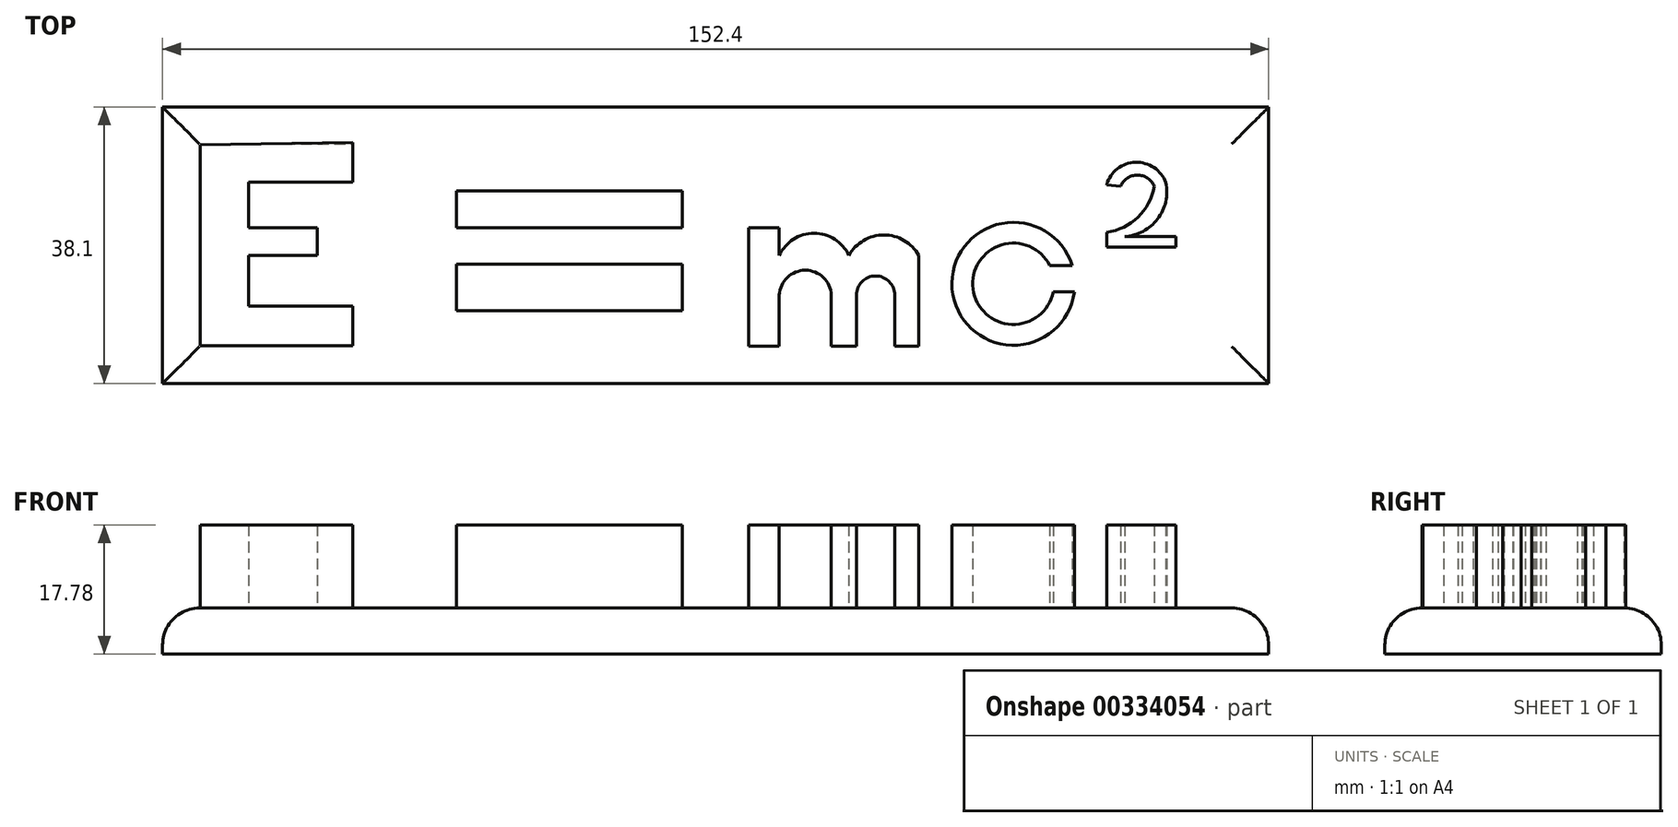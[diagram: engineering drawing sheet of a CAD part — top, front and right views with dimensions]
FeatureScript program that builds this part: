
annotation { "Feature Type Name" : "Feature", "Feature Type Description" : "" }
export const myFeature = defineFeature(function(context is Context, id is Id, definition is map)
    precondition{}
    {
        {
            var Q0;
            Q0=qCreatedBy(makeId("Top.planeOp"),FACE);
            var sketch = newSketch(context, id + "F0", { "sketchPlane" : qUnion([Q0])});
            skLineSegment(sketch, "E0", {"start": v(-76.78, -21.49) * mm, "end": v(75.62, -21.49) * mm});
            skLineSegment(sketch, "E1", {"start": v(-76.78, -21.49) * mm, "end": v(-76.78, 16.61) * mm});
            skLineSegment(sketch, "E2", {"start": v(-76.78, 16.61) * mm, "end": v(75.62, 16.61) * mm});
            skLineSegment(sketch, "E3", {"start": v(75.62, 16.61) * mm, "end": v(75.62, -21.49) * mm});
            skSolve(sketch);
        }
        {
            var Q0;
            Q0 = qSketchRegion(id + "F0", true);
            extrude(context, id + "F1", {"entities" : qUnion([Q0]), "depth" : 6.35 * mm});
        }
        {
            var Q0;
            Q0=makeQuery(id+"F1.opExtrude","CAP_FACE",FACE,{"disambiguationData":[OSD([sQuery(id+"F0.wireOp",EDGE,"E0"),sQuery(id+"F0.wireOp",EDGE,"E1"),sQuery(id+"F0.wireOp",EDGE,"E2"),sQuery(id+"F0.wireOp",EDGE,"E3")])],"isStart":false});
            fillet(context, id + "F2", {"entities" : qUnion([Q0]), "radius" : 5.08 * mm, "tangentPropagation" : true, "allowEdgeOverflow" : false});
        }
        {
            var Q0;
            Q0=makeQuery(id+"F1.opExtrude","CAP_FACE",FACE,{"disambiguationData":[OSD([sQuery(id+"F0.wireOp",EDGE,"E0"),sQuery(id+"F0.wireOp",EDGE,"E1"),sQuery(id+"F0.wireOp",EDGE,"E2"),sQuery(id+"F0.wireOp",EDGE,"E3")])],"isStart":false});
            var sketch = newSketch(context, id + "F3", { "sketchPlane" : qUnion([Q0])});
            skLineSegment(sketch, "E4", {"start": v(-71.61, 11.43) * mm, "end": v(-71.61, -16.3) * mm});
            skLineSegment(sketch, "E5", {"start": v(-71.61, -16.3) * mm, "end": v(-50.58, -16.3) * mm});
            skLineSegment(sketch, "E6", {"start": v(-50.58, -16.3) * mm, "end": v(-50.58, -10.82) * mm});
            skLineSegment(sketch, "E7", {"start": v(-50.58, -10.82) * mm, "end": v(-64.9, -10.82) * mm});
            skLineSegment(sketch, "E8", {"start": v(-64.9, -10.82) * mm, "end": v(-64.9, -3.81) * mm});
            skLineSegment(sketch, "E9", {"start": v(-64.9, -3.81) * mm, "end": v(-55.46, -3.81) * mm});
            skLineSegment(sketch, "E10", {"start": v(-55.46, -3.81) * mm, "end": v(-55.46, 0) * mm});
            skLineSegment(sketch, "E11", {"start": v(-64.9, 0) * mm, "end": v(-64.9, 6.25) * mm});
            skLineSegment(sketch, "E12", {"start": v(-64.9, 6.25) * mm, "end": v(-50.58, 6.25) * mm});
            skLineSegment(sketch, "E13", {"start": v(-50.58, 6.25) * mm, "end": v(-50.58, 11.73) * mm});
            skLineSegment(sketch, "E14", {"start": v(-50.58, 11.73) * mm, "end": v(-71.61, 11.43) * mm});
            skLineSegment(sketch, "E15", {"start": v(-64.9, 0) * mm, "end": v(-55.46, 0) * mm});
            skSolve(sketch);
        }
        {
            var Q0;
            Q0 = qSketchRegion(id + "F3", true);
            extrude(context, id + "F4", {"entities" : qUnion([Q0]), "operationType" : NewBodyOperationType.ADD, "depth" : 11.43 * mm});
        }
        {
            var Q0;
            Q0=makeQuery(id+"F1.opExtrude","CAP_FACE",FACE,{"disambiguationData":[OSD([sQuery(id+"F0.wireOp",EDGE,"E0"),sQuery(id+"F0.wireOp",EDGE,"E1"),sQuery(id+"F0.wireOp",EDGE,"E2"),sQuery(id+"F0.wireOp",EDGE,"E3")])],"isStart":false});
            var sketch = newSketch(context, id + "F5", { "sketchPlane" : qUnion([Q0])});
            skLineSegment(sketch, "E16", {"start": v(-36.26, 5.03) * mm, "end": v(-36.26, 0) * mm});
            skLineSegment(sketch, "E17", {"start": v(-36.26, 5.03) * mm, "end": v(-5.17, 5.03) * mm});
            skLineSegment(sketch, "E18", {"start": v(-5.17, 5.03) * mm, "end": v(-5.17, 0) * mm});
            skLineSegment(sketch, "E19", {"start": v(-5.17, 0) * mm, "end": v(-36.26, 0) * mm});
            skLineSegment(sketch, "E20", {"start": v(-36.26, -5.03) * mm, "end": v(-5.17, -5.03) * mm});
            skLineSegment(sketch, "E21", {"start": v(-5.17, -5.03) * mm, "end": v(-5.17, -11.43) * mm});
            skLineSegment(sketch, "E22", {"start": v(-5.17, -11.43) * mm, "end": v(-36.26, -11.43) * mm});
            skLineSegment(sketch, "E23", {"start": v(-36.26, -11.43) * mm, "end": v(-36.26, -5.03) * mm});
            skSolve(sketch);
        }
        {
            var Q0;
            Q0 = qSketchRegion(id + "F5", true);
            extrude(context, id + "F6", {"entities" : qUnion([Q0]), "operationType" : NewBodyOperationType.ADD, "depth" : 11.43 * mm});
        }
        {
            var Q0;
            Q0=makeQuery(id+"F1.opExtrude","CAP_FACE",FACE,{"disambiguationData":[OSD([sQuery(id+"F0.wireOp",EDGE,"E0"),sQuery(id+"F0.wireOp",EDGE,"E1"),sQuery(id+"F0.wireOp",EDGE,"E2"),sQuery(id+"F0.wireOp",EDGE,"E3")])],"isStart":false});
            var sketch = newSketch(context, id + "F7", { "sketchPlane" : qUnion([Q0])});
            skLineSegment(sketch, "E24", {"start": v(3.99, -16.32) * mm, "end": v(3.99, -0.03) * mm});
            skLineSegment(sketch, "E25", {"start": v(8.2, -0.03) * mm, "end": v(8.2, -3.83) * mm});
            skLineSegment(sketch, "E26", {"start": v(8.2, -16.32) * mm, "end": v(8.2, -9.3) * mm});
            skArc(sketch, "E27", {"start": v(17.78, -3.83) * mm, "mid": v(12.99, -0.8) * mm, "end": v(8.2, -3.83) * mm});
            skArc(sketch, "E28", {"start": v(27.41, -3.83) * mm, "mid": v(22.6, -1.02) * mm, "end": v(17.78, -3.83) * mm});
            skLineSegment(sketch, "E29", {"start": v(27.41, -3.83) * mm, "end": v(27.41, -16.35) * mm});
            skArc(sketch, "E30", {"start": v(15.37, -9.3) * mm, "mid": v(11.78, -5.88) * mm, "end": v(8.2, -9.3) * mm});
            skLineSegment(sketch, "E31", {"start": v(15.37, -9.3) * mm, "end": v(15.37, -16.34) * mm});
            skLineSegment(sketch, "E32", {"start": v(18.81, -16.34) * mm, "end": v(18.81, -9.3) * mm});
            skArc(sketch, "E33", {"start": v(24.1, -9.3) * mm, "mid": v(21.46, -6.67) * mm, "end": v(18.81, -9.3) * mm});
            skLineSegment(sketch, "E34", {"start": v(24.1, -9.3) * mm, "end": v(24.1, -16.35) * mm});
            skLineSegment(sketch, "E35", {"start": v(3.99, -16.32) * mm, "end": v(8.2, -16.32) * mm});
            skLineSegment(sketch, "E36", {"start": v(15.37, -16.34) * mm, "end": v(18.81, -16.34) * mm});
            skLineSegment(sketch, "E37", {"start": v(24.1, -16.35) * mm, "end": v(27.41, -16.35) * mm});
            skLineSegment(sketch, "E38", {"start": v(3.99, -0.03) * mm, "end": v(8.2, -0.03) * mm});
            skSolve(sketch);
        }
        {
            var Q0;
            Q0 = qSketchRegion(id + "F7", true);
            extrude(context, id + "F8", {"entities" : qUnion([Q0]), "operationType" : NewBodyOperationType.ADD, "depth" : 11.43 * mm});
        }
        {
            var Q0;
            {var subQ8=sQuery(id+"F0.wireOp",EDGE,"E3");var subQ9=sQuery(id+"F0.wireOp",EDGE,"E2");var subQ14=sQuery(id+"F0.wireOp",EDGE,"E1");var subQ15=sQuery(id+"F0.wireOp",EDGE,"E0");Q0=makeQuery(id+"F8.boolean.opBoolean","SPLIT",FACE,{"disambiguationData":[TD([makeQuery(id+"F2.opFillet","BLEND_FACE",FACE,{"disambiguationData":[OSD([subQ14])]})])],"derivedFrom":makeQuery(id+"F1.opExtrude","CAP_FACE",FACE,{"disambiguationData":[OSD([subQ15,subQ14,subQ9,subQ8])],"isStart":false})});}
            var sketch = newSketch(context, id + "F9", { "sketchPlane" : qUnion([Q0])});
            skArc(sketch, "E39", {"start": v(48.55, -5.24) * mm, "mid": v(32.01, -8.45) * mm, "end": v(48.85, -8.88) * mm});
            skArc(sketch, "E40", {"start": v(45.47, -5.24) * mm, "mid": v(34.9, -8.47) * mm, "end": v(45.95, -8.88) * mm});
            skLineSegment(sketch, "E41", {"start": v(45.95, -8.88) * mm, "end": v(48.85, -8.88) * mm});
            skLineSegment(sketch, "E42", {"start": v(45.47, -5.24) * mm, "end": v(48.55, -5.24) * mm});
            skSolve(sketch);
        }
        {
            var Q0;
            Q0 = qSketchRegion(id + "F9", true);
            extrude(context, id + "F10", {"entities" : qUnion([Q0]), "operationType" : NewBodyOperationType.ADD, "depth" : 11.43 * mm});
        }
        {
            var Q0;
            {var subQ8=sQuery(id+"F0.wireOp",EDGE,"E3");var subQ9=sQuery(id+"F0.wireOp",EDGE,"E2");var subQ14=sQuery(id+"F0.wireOp",EDGE,"E1");var subQ15=sQuery(id+"F0.wireOp",EDGE,"E0");Q0=makeQuery(id+"F8.boolean.opBoolean","SPLIT",FACE,{"disambiguationData":[TD([makeQuery(id+"F2.opFillet","BLEND_FACE",FACE,{"disambiguationData":[OSD([subQ14])]})])],"derivedFrom":makeQuery(id+"F1.opExtrude","CAP_FACE",FACE,{"disambiguationData":[OSD([subQ15,subQ14,subQ9,subQ8])],"isStart":false})});}
            var sketch = newSketch(context, id + "F11", { "sketchPlane" : qUnion([Q0])});
            skArc(sketch, "E43", {"start": v(61.45, 6.19) * mm, "mid": v(57.28, 8.99) * mm, "end": v(53.3, 5.9) * mm});
            skArc(sketch, "E44", {"start": v(55.79, -1.24) * mm, "mid": v(60.32, 1.18) * mm, "end": v(61.45, 6.19) * mm});
            skLineSegment(sketch, "E45", {"start": v(55.79, -1.24) * mm, "end": v(62.84, -1.24) * mm});
            skLineSegment(sketch, "E46", {"start": v(62.84, -1.24) * mm, "end": v(62.84, -2.71) * mm});
            skLineSegment(sketch, "E47", {"start": v(62.84, -2.71) * mm, "end": v(53.3, -2.71) * mm});
            skLineSegment(sketch, "E48", {"start": v(53.3, -2.71) * mm, "end": v(53.3, -0.64) * mm});
            skArc(sketch, "E49", {"start": v(53.3, -0.64) * mm, "mid": v(57.62, 1.43) * mm, "end": v(59.84, 5.68) * mm});
            skArc(sketch, "E50", {"start": v(59.84, 5.68) * mm, "mid": v(57.54, 7.24) * mm, "end": v(55.23, 5.68) * mm});
            skLineSegment(sketch, "E51", {"start": v(53.3, 5.9) * mm, "end": v(55.23, 5.68) * mm});
            skSolve(sketch);
        }
        {
            var Q0;
            Q0 = qSketchRegion(id + "F11", true);
            extrude(context, id + "F12", {"entities" : qUnion([Q0]), "operationType" : NewBodyOperationType.ADD, "depth" : 11.43 * mm});
        }
    });
